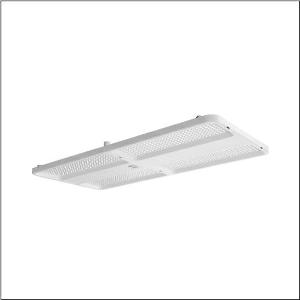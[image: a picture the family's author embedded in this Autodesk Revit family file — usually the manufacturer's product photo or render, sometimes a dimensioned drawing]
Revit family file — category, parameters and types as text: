
# Revit family: highbay_21_maxi_52hn12db4mda03
name_source: partatom
category: Lighting Fixtures
units: mm (PartAtom-declared; Revit-internal decimal feet)

## family parameters
Cut with Voids When Loaded = No
Host = Face
Light Source = No
Part Type = Normal
Room Calculation Point = No
Round Connector Dimension = Use Diameter
Shared = No

## types (1)
- --- (1 x LED, 28000 lm, 144 W, 4000K)
    Apparent Load = 144 VA
    CIE Flux Codes = 90 98 100 100 100
    Color Rendering = 80
    Color Temperature = 4000K
    Default Elevation = 1800 mm
    Description = high bay luminaire Highbay 21 maxi; direct symmetric wide distribution, light control with lens of PMMA; UGR ≤ 22 (X = 4H | Y = 8H | S = 0.25H | reflection values 70/50/20); luminous flux: 28.000lm; light colour: 840, colour temperature: 4000K, MacAdam ≤ 3 SDCM (initial), colour rendering: CRI > 80; luminous efficacy: 194,4lm/W; rated service life: 75.000h (L80) at AT= ta max; control: DALI 2; for wired networking: open and standardized DALI2 interface enables full flexibility and future-proofing for changes in use or functional adaptation through individual programming; multi-sensor luminaire consisting of a DALI2 multi-sensor and DALI2 ECG; multi-sensor luminaire for wired connection to a DALI2 application controller (e.g., SITECO Connect 11 or 21); can also be connected to existing on-site lighting or building automation systems upon request; integrated DALI2 sensor certified according to IEC 62386, Parts 101, 103, 303, and 304; integrated DALI2 ECG provides luminaire data (according to IEC 62386, Part 251), energy data (Part 252), and monitoring and analytics data (Part 253) to higher-level systems for further processing; luminaire with PIR sensor (passive-infrared); with light sensor; luminaire connection: terminal, 5-pole, max. 2.5mm² (cable entry for one cable, Ø 8.5..16mm); mains connection: 230..240V, AC 50/60Hz; connected load: 144W; protection rating (complete): IP65; insulation class (complete): insulation class I (protective earthing); protection symbol: D; certification: CE, UKCA; internal wiring halogen-free; luminaire LABS conformity tested according to VDMA 24364:2018-05; Suitable for use in the food industry according to the specifications of IFS-Food, HACCP and/or BRC; housing frame of high-performance plastic PA6, matt traffic white (RAL 9016); cover of PMMA; dimension (LxWxH): 946 x 442 x 72mm; permissible operating ambient temperature: -20..+45°C (reducing of maximum allowable ambient temperature of 5°C with ceiling mounting); packaging unit: 1 piece; (delivery without accessories; please order mounting accessories separately)
    Height = 72 mm  [stored 0.23622 ft]
    Lamp = 1 x LED
    Lamp Light Flux = 28000 lm
    Lamp Power = 144 W
    Lamp count = 1
    Length = 946 mm
    Luminous efficacy = 194 lm/W
    Manufacturer = Siteco
    ModVariant = No
    Model = 52HN12DB4MDA03
    Mounting Place = Ceiling
    Mounting Type = Pendant
    Number of Poles = 1
    OnlyDefault = Yes
    Power Factor = 1
    Product Name = Highbay 21 maxi
    Product group = high bay luminaire
    ProductGroupID = 902
    Protection Class = Protection class I
    Protection Degree = IP 65
    RLX_Detail_Level = 1
    RLX_Emergency_Light_Flux = 0 lm
    RLX_Emergency_Type = 0
    RLX_Emergency_Type_DB = No
    RlxData = <blob elided: 128089 chars, md5=1fd6dd5d>
    Socket = socket
    Standby Power = 0 W
    System Light Flux = 27999 lm
    System Power = 144 W
    Type Comments = factory setting: luminous flux: 100 % | dim-lin: 254 | 668 mA
    Type Image = l_1363267.jpg
    URL = http://relux.com
    VarID = @adj_013793
    Voltage = 0 V
    Weight = 0.00 kg
    Width = 442 mm

note: [stored X ft] marks values corroborated as IEEE doubles in the binary element streams (Revit-internal decimal feet)

## geometry (parser evidence)
native form markers: Blend x4, Sweep x11
no freeform markers — native parametric forms only
